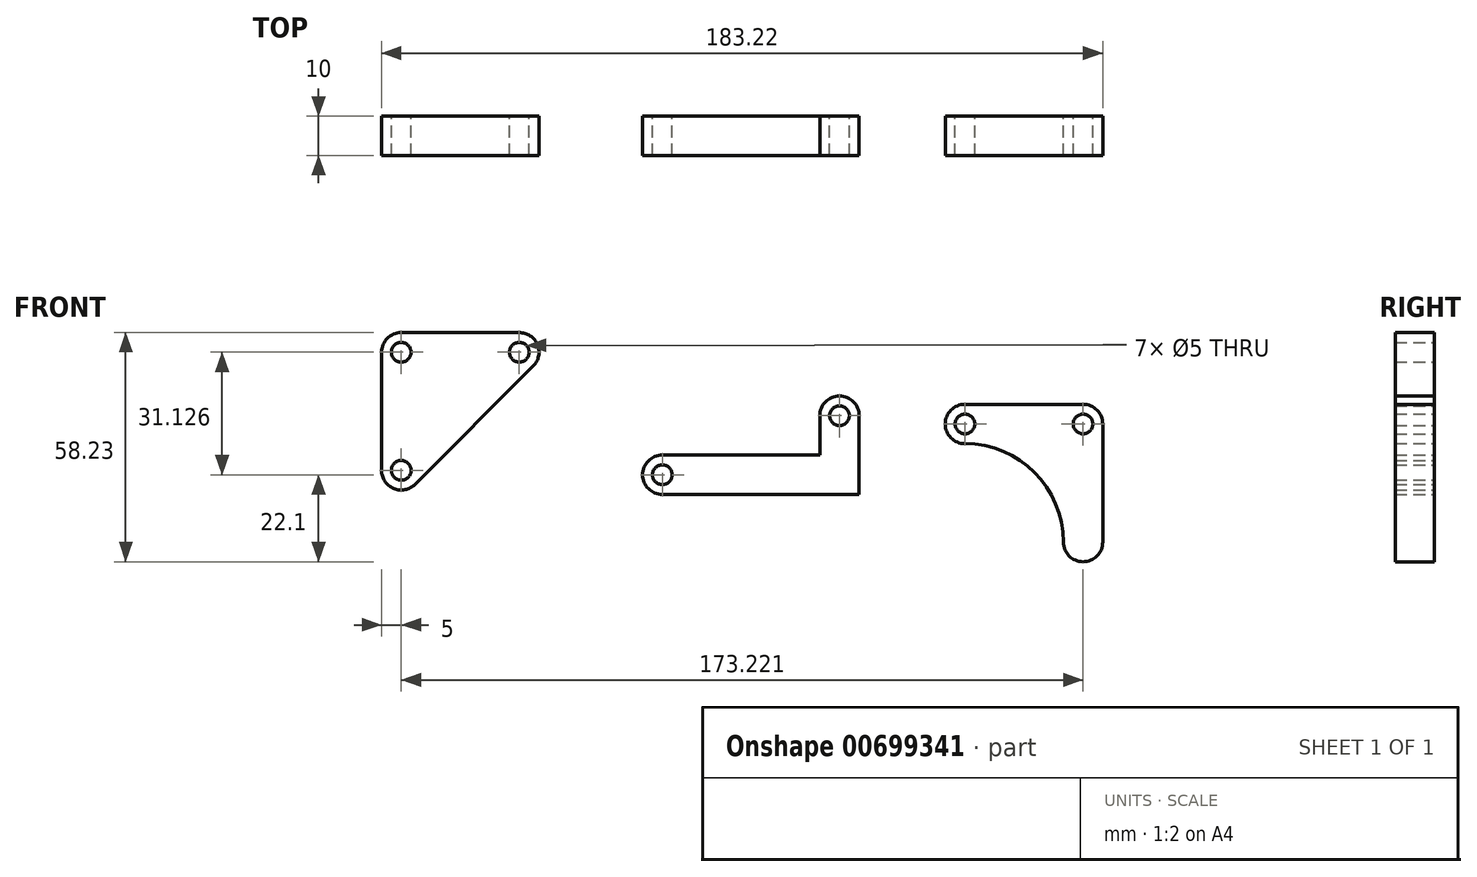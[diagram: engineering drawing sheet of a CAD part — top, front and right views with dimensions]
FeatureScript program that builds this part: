
annotation { "Feature Type Name" : "Feature", "Feature Type Description" : "" }
export const myFeature = defineFeature(function(context is Context, id is Id, definition is map)
    precondition{}
    {
        {
            var Q0;
            Q0=qCreatedBy(makeId("Front.planeOp"),FACE);
            var sketch = newSketch(context, id + "F0", { "sketchPlane" : qUnion([Q0])});
            skLineSegment(sketch, "E0", {"start": v(0, 0) * mm, "end": v(0, 20) * mm});
            skLineSegment(sketch, "E1", {"start": v(-10, 20) * mm, "end": v(-10, 10) * mm});
            skLineSegment(sketch, "E2", {"start": v(-10, 10) * mm, "end": v(-50, 10) * mm});
            skLineSegment(sketch, "E3", {"start": v(-50, 0) * mm, "end": v(0, 0) * mm});
            skArc(sketch, "E4", {"start": v(0, 20) * mm, "mid": v(-5, 25) * mm, "end": v(-10, 20) * mm});
            skArc(sketch, "E5", {"start": v(-50, 10) * mm, "mid": v(-55, 5) * mm, "end": v(-50, 0) * mm});
            skCircle(sketch, "E6", {"center": v(-50, 5) * mm, "radius": 2.5 * mm});
            skCircle(sketch, "E7", {"center": v(-5, 20) * mm, "radius": 2.5 * mm});
            skSolve(sketch);
        }
        {
            var Q0;
            Q0=makeQuery(id+"F0.imprint","IMPRINT",FACE,{"disambiguationData":[TD([[makeQuery(id+"F0.imprint","IMPRINT",EDGE,{"derivedFrom":sQuery(id+"F0.wireOp",EDGE,"E0")}),1.0]])]});
            extrude(context, id + "F1", {"entities" : qUnion([Q0]), "depth" : 10 * mm, "offsetDistance" : 25 * mm, "symmetric" : true});
        }
        {
            var Q0;
            Q0=qCreatedBy(makeId("Front.planeOp"),FACE);
            var sketch = newSketch(context, id + "F2", { "sketchPlane" : qUnion([Q0])});
            skLineSegment(sketch, "E8", {"start": v(-121.34, 6.13) * mm, "end": v(-121.34, 36.13) * mm});
            skLineSegment(sketch, "E9", {"start": v(-116.34, 41.13) * mm, "end": v(-86.34, 41.13) * mm});
            skLineSegment(sketch, "E10", {"start": v(-82.8, 32.6) * mm, "end": v(-112.8, 2.6) * mm});
            skArc(sketch, "E11", {"start": v(-116.34, 41.13) * mm, "mid": v(-119.88, 39.66) * mm, "end": v(-121.34, 36.13) * mm});
            skArc(sketch, "E12", {"start": v(-121.34, 6.13) * mm, "mid": v(-118.25, 1.5) * mm, "end": v(-112.8, 2.6) * mm});
            skArc(sketch, "E13", {"start": v(-82.8, 32.6) * mm, "mid": v(-81.72, 38.04) * mm, "end": v(-86.34, 41.13) * mm});
            skCircle(sketch, "E14", {"center": v(-116.34, 36.13) * mm, "radius": 2.5 * mm});
            skCircle(sketch, "E15", {"center": v(-116.34, 6.13) * mm, "radius": 2.5 * mm});
            skCircle(sketch, "E16", {"center": v(-86.34, 36.13) * mm, "radius": 2.5 * mm});
            skSolve(sketch);
        }
        {
            var Q0;
            Q0 = qSketchRegion(id + "F2", true);
            extrude(context, id + "F3", {"entities" : qUnion([Q0]), "depth" : 10 * mm, "offsetDistance" : 25 * mm, "symmetric" : true});
        }
        {
            var Q0;
            Q0=qCreatedBy(makeId("Front.planeOp"),FACE);
            var sketch = newSketch(context, id + "F4", { "sketchPlane" : qUnion([Q0])});
            skLineSegment(sketch, "E17", {"start": v(26.88, 22.9) * mm, "end": v(56.88, 22.9) * mm});
            skLineSegment(sketch, "E18", {"start": v(61.88, 17.9) * mm, "end": v(61.88, -12.1) * mm});
            skArc(sketch, "E19", {"start": v(26.88, 22.9) * mm, "mid": v(21.88, 17.9) * mm, "end": v(26.88, 12.9) * mm});
            skArc(sketch, "E20", {"start": v(51.88, -12.1) * mm, "mid": v(56.88, -17.1) * mm, "end": v(61.88, -12.1) * mm});
            skArc(sketch, "E21", {"start": v(61.88, 17.9) * mm, "mid": v(60.42, 21.44) * mm, "end": v(56.88, 22.9) * mm});
            skArc(sketch, "E22", {"start": v(51.88, -12.1) * mm, "mid": v(44.56, 5.58) * mm, "end": v(26.88, 12.9) * mm});
            skCircle(sketch, "E23", {"center": v(26.88, 17.9) * mm, "radius": 2.5 * mm});
            skCircle(sketch, "E24", {"center": v(56.88, 17.9) * mm, "radius": 2.5 * mm});
            skSolve(sketch);
        }
        {
            var Q0;
            Q0 = qSketchRegion(id + "F4", true);
            extrude(context, id + "F5", {"entities" : qUnion([Q0]), "depth" : 10 * mm, "offsetDistance" : 25 * mm, "symmetric" : true});
        }
    });
